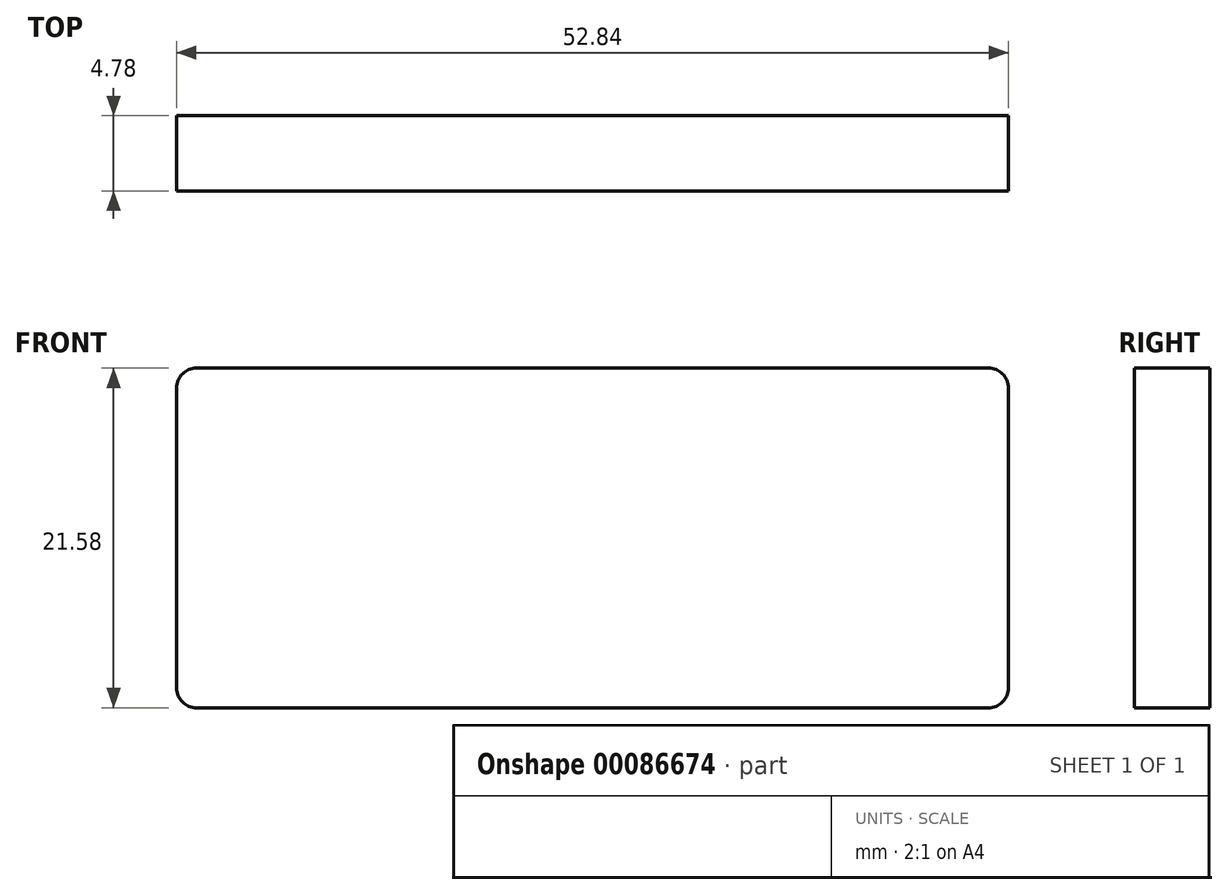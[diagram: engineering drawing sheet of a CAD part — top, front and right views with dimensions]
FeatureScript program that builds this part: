
annotation { "Feature Type Name" : "Feature", "Feature Type Description" : "" }
export const myFeature = defineFeature(function(context is Context, id is Id, definition is map)
    precondition{}
    {
        {
            var Q0;
            Q0=qCreatedBy(makeId("Front.planeOp"),FACE);
            var sketch = newSketch(context, id + "F0", { "sketchPlane" : qUnion([Q0])});
            skLineSegment(sketch, "E0.bottom", {"start": v(-26.42, 10.8) * mm, "end": v(26.42, 10.8) * mm});
            skLineSegment(sketch, "E0.top", {"start": v(-26.42, -10.8) * mm, "end": v(26.42, -10.8) * mm});
            skLineSegment(sketch, "E0.left", {"start": v(-26.42, 10.8) * mm, "end": v(-26.42, -10.8) * mm});
            skLineSegment(sketch, "E0.right", {"start": v(26.42, 10.8) * mm, "end": v(26.42, -10.8) * mm});
            skPoint(sketch, "E0.middle", {"position": v(0, 0) * mm});
            skSolve(sketch);
        }
        {
            var Q0;
            Q0=makeQuery(id+"F0.imprint","IMPRINT",FACE,{"disambiguationData":[TD([[makeQuery(id+"F0.imprint","IMPRINT",EDGE,{"derivedFrom":sQuery(id+"F0.wireOp",EDGE,"E0.bottom")}),-1.0]])]});
            extrude(context, id + "F1", {"entities" : qUnion([Q0]), "depth" : 4.78 * mm});
        }
        {
            var Q0;
            Q0=makeQuery(id+"F1.opExtrude","SWEPT_EDGE",EDGE,{"disambiguationData":[OSD([sQuery(id+"F0.wireOp",EDGE,"E0.bottom"),sQuery(id+"F0.wireOp",EDGE,"E0.left")])]});
            var Q1;
            Q1=makeQuery(id+"F1.opExtrude","SWEPT_EDGE",EDGE,{"disambiguationData":[OSD([sQuery(id+"F0.wireOp",EDGE,"E0.bottom"),sQuery(id+"F0.wireOp",EDGE,"E0.right")])]});
            var Q2;
            Q2=makeQuery(id+"F1.opExtrude","SWEPT_EDGE",EDGE,{"disambiguationData":[OSD([sQuery(id+"F0.wireOp",EDGE,"E0.top"),sQuery(id+"F0.wireOp",EDGE,"E0.right")])]});
            var Q3;
            Q3=makeQuery(id+"F1.opExtrude","SWEPT_EDGE",EDGE,{"disambiguationData":[OSD([sQuery(id+"F0.wireOp",EDGE,"E0.top"),sQuery(id+"F0.wireOp",EDGE,"E0.left")])]});
            fillet(context, id + "F2", {"entities" : qUnion([Q0, Q1, Q2, Q3]), "radius" : 1.27 * mm, "tangentPropagation" : true, "allowEdgeOverflow" : false});
        }
        {
            var Q0;
            Q0=makeQuery(id+"F1.opExtrude","SWEPT_BODY",BODY,{"disambiguationData":[OSD([sQuery(id+"F0.wireOp",EDGE,"E0.bottom"),sQuery(id+"F0.wireOp",EDGE,"E0.top"),sQuery(id+"F0.wireOp",EDGE,"E0.left"),sQuery(id+"F0.wireOp",EDGE,"E0.right")])]});
            transform(context, id + "F3", {"entities" : qUnion([Q0]), "transformType" : TransformType.TRANSLATION_3D, "dx" : 0 * mm, "dy" : 0 * mm, "dz" : 0 * mm, "makeCopy" : true});
        }
        {
            var Q0;
            Q0=makeQuery(id+"F3.opPattern","COPY",BODY,{"derivedFrom":makeQuery(id+"F1.opExtrude","SWEPT_BODY",BODY,{"disambiguationData":[OSD([sQuery(id+"F0.wireOp",EDGE,"E0.bottom"),sQuery(id+"F0.wireOp",EDGE,"E0.top"),sQuery(id+"F0.wireOp",EDGE,"E0.left"),sQuery(id+"F0.wireOp",EDGE,"E0.right")])]}),"instanceName":"1"});
            deleteBodies(context, id + "F4", {"entities" : qUnion([Q0])});
        }
    });
